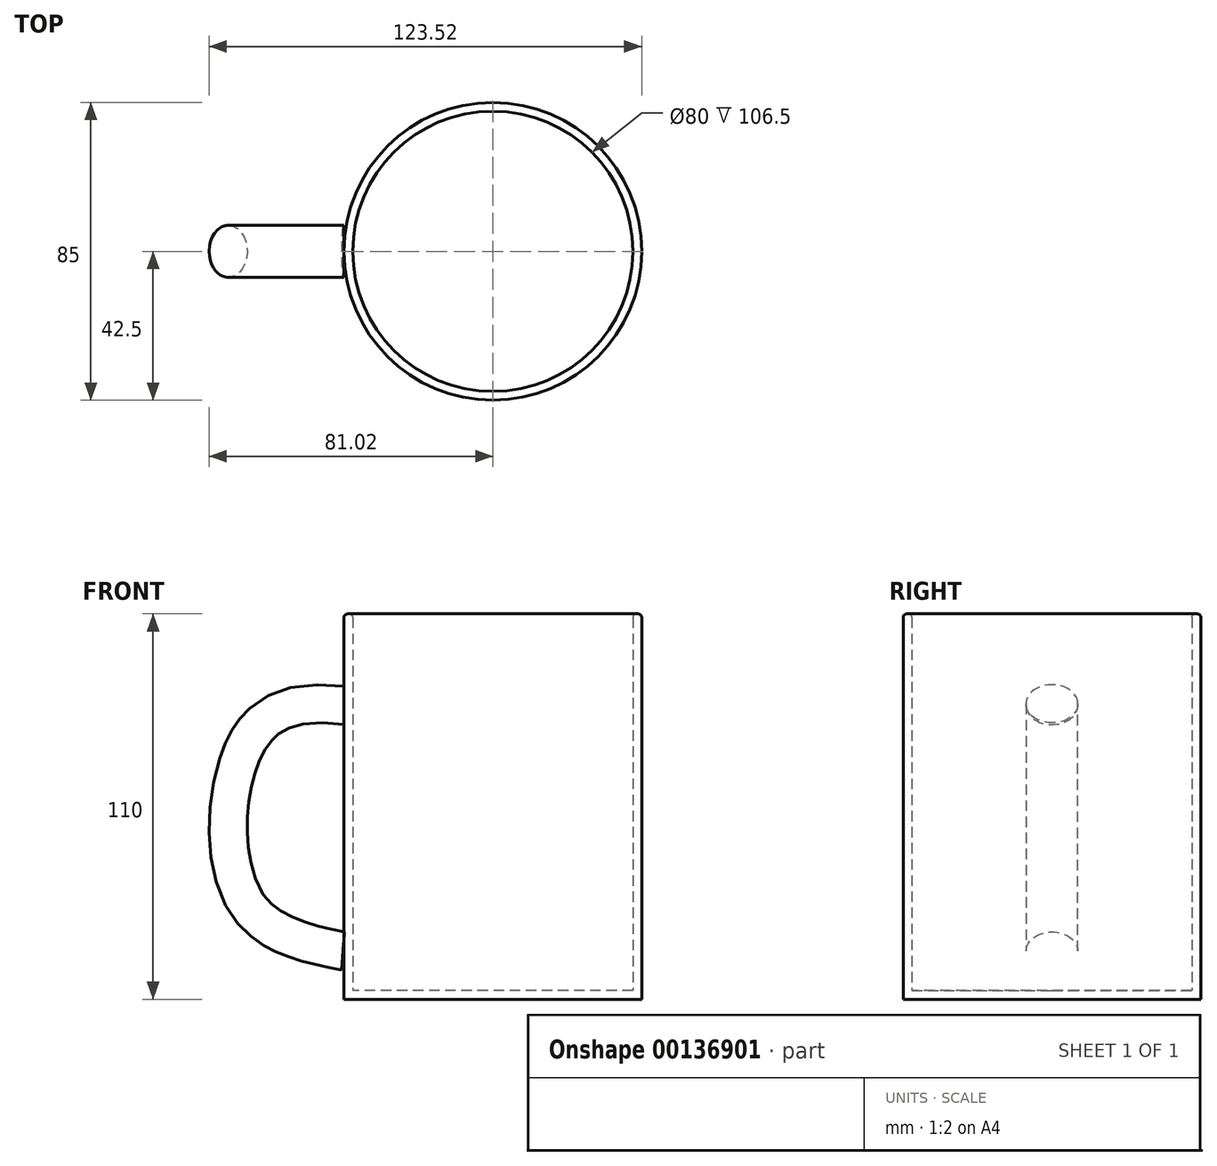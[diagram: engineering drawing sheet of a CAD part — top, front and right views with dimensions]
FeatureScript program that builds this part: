
annotation { "Feature Type Name" : "Feature", "Feature Type Description" : "" }
export const myFeature = defineFeature(function(context is Context, id is Id, definition is map)
    precondition{}
    {
        {
            var Q0;
            Q0=qCreatedBy(makeId("Top.planeOp"),FACE);
            var sketch = newSketch(context, id + "F0", { "sketchPlane" : qUnion([Q0])});
            skCircle(sketch, "E0", {"center": v(0, 0) * mm, "radius": 42.5 * mm});
            skLineSegment(sketch, "E1", {"start": v(0, 0) * mm, "end": v(42.5, 0) * mm});
            skSolve(sketch);
        }
        {
            var Q0;
            Q0=makeQuery(id+"F0.imprint","IMPRINT",FACE,{"disambiguationData":[TD([[makeQuery(id+"F0.imprint","IMPRINT",EDGE,{"derivedFrom":sQuery(id+"F0.wireOp",EDGE,"E0")}),1.0]])]});
            extrude(context, id + "F1", {"entities" : qUnion([Q0]), "depth" : 110 * mm});
        }
        {
            var Q0;
            Q0=qCreatedBy(makeId("Right.planeOp"),FACE);
            cPlane(context, id + "F2", {"entities" : qUnion([Q0]), "cplaneType" : CPlaneType.OFFSET, "offset" : 42.5 * mm, "oppositeDirection" : true, "width" : 150 * mm, "height" : 150 * mm});
        }
        {
            var Q0;
            Q0=makeQuery(id+"F1.opExtrude","CAP_FACE",FACE,{"disambiguationData":[OSD([sQuery(id+"F0.wireOp",EDGE,"E0")])],"isStart":false});
            shell(context, id + "F3", {"entities" : qUnion([Q0]), "thickness" : 2.5 * mm});
        }
        {
            var Q0;
            Q0=makeQuery(id+"F1.opExtrude","CAP_EDGE",EDGE,{"disambiguationData":[OSD([sQuery(id+"F0.wireOp",EDGE,"E0")])],"isStart":false});
            var Q1;
            {var subQ0=sQuery(id+"F0.wireOp",EDGE,"E0");Q1=makeQuery(id+"F3.opShell","OFFSET_EDGE",EDGE,{"disambiguationData":[OSD([subQ0]),TDD([makeQuery(id+"F1.opExtrude","CAP_EDGE",EDGE,{"disambiguationData":[OSD([subQ0])],"isStart":false})])]});}
            fillet(context, id + "F4", {"entities" : qUnion([Q0, Q1]), "radius" : 1 * mm, "tangentPropagation" : true, "allowEdgeOverflow" : false});
        }
        {
            var Q0;
            Q0=qCreatedBy(makeId("Front.planeOp"),FACE);
            var sketch = newSketch(context, id + "F5", { "sketchPlane" : qUnion([Q0])});
            skFitSpline(sketch, "E2", {"points": [v(-42.59, 83.88) * mm, v(-70.34, 72.96) * mm, v(-70.78, 28.03) * mm, v(-42.7, 13.77) * mm], "startDerivative": vector(-133.97, 16.75) * mm, "endDerivative": vector(105.37, -21.32) * mm});
            skSolve(sketch);
        }
        {
            var Q0;
            Q0=qCreatedBy(id+"F2.planeOp",FACE);
            var sketch = newSketch(context, id + "F6", { "sketchPlane" : qUnion([Q0])});
            skEllipse(sketch, "E3", {"center": v(0, 83.88) * mm, "majorRadius": 7.4 * mm, "minorRadius": 5.5 * mm, "majorAxis": v(-1, 0)});
            skSolve(sketch);
        }
        {
            var Q0;
            Q0=makeQuery(id+"F6.imprint","IMPRINT",FACE,{"disambiguationData":[TD([[makeQuery(id+"F6.imprint","IMPRINT",EDGE,{"derivedFrom":sQuery(id+"F6.wireOp",EDGE,"E3")}),1.0]])]});
            var Q1;
            Q1=sQuery(id+"F5.wireOp",EDGE,"E2");
            sweep(context, id + "F7", {"profiles" : qUnion([Q0]), "path" : qUnion([Q1])});
        }
    });
